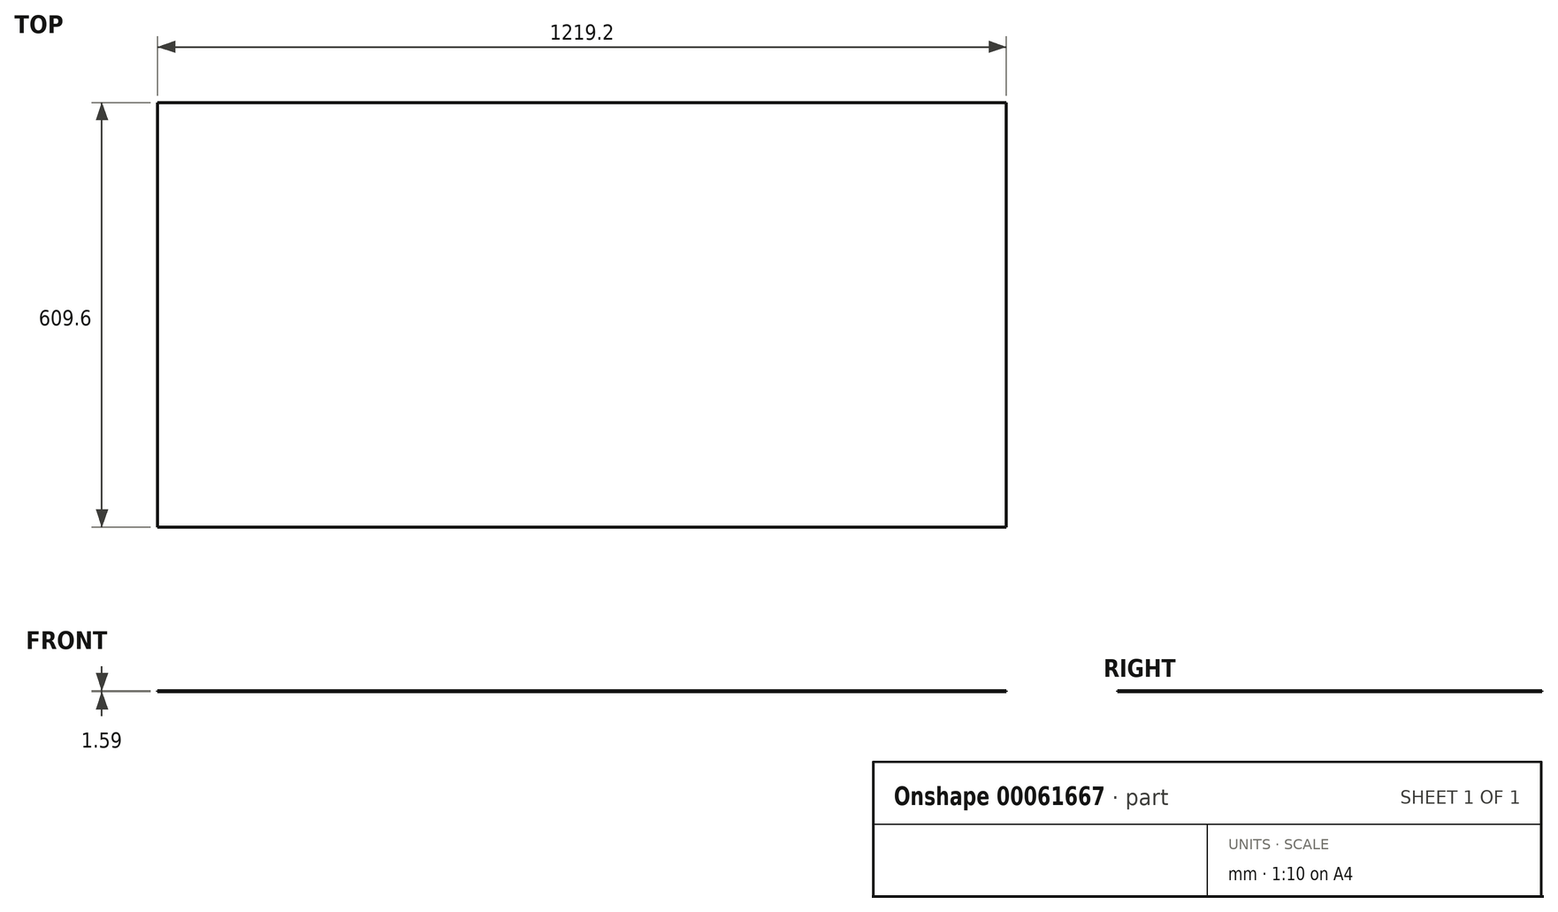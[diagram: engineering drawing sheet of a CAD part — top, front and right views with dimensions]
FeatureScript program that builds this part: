
annotation { "Feature Type Name" : "Feature", "Feature Type Description" : "" }
export const myFeature = defineFeature(function(context is Context, id is Id, definition is map)
    precondition{}
    {
        {
            var Q0;
            Q0=qCreatedBy(makeId("Top.planeOp"),FACE);
            var sketch = newSketch(context, id + "F0", { "sketchPlane" : qUnion([Q0])});
            skLineSegment(sketch, "E0.bottom", {"start": v(0, 0) * mm, "end": v(1219.2, 0) * mm});
            skLineSegment(sketch, "E0.top", {"start": v(0, 609.6) * mm, "end": v(1219.2, 609.6) * mm});
            skLineSegment(sketch, "E0.left", {"start": v(0, 0) * mm, "end": v(0, 609.6) * mm});
            skLineSegment(sketch, "E0.right", {"start": v(1219.2, 0) * mm, "end": v(1219.2, 609.6) * mm});
            skSolve(sketch);
        }
        {
            var Q0;
            Q0=makeQuery(id+"F0.imprint","IMPRINT",FACE,{"disambiguationData":[TD([[makeQuery(id+"F0.imprint","IMPRINT",EDGE,{"derivedFrom":sQuery(id+"F0.wireOp",EDGE,"E0.bottom")}),1.0]])]});
            extrude(context, id + "F1", {"entities" : qUnion([Q0]), "depth" : 1.59 * mm});
        }
    });
